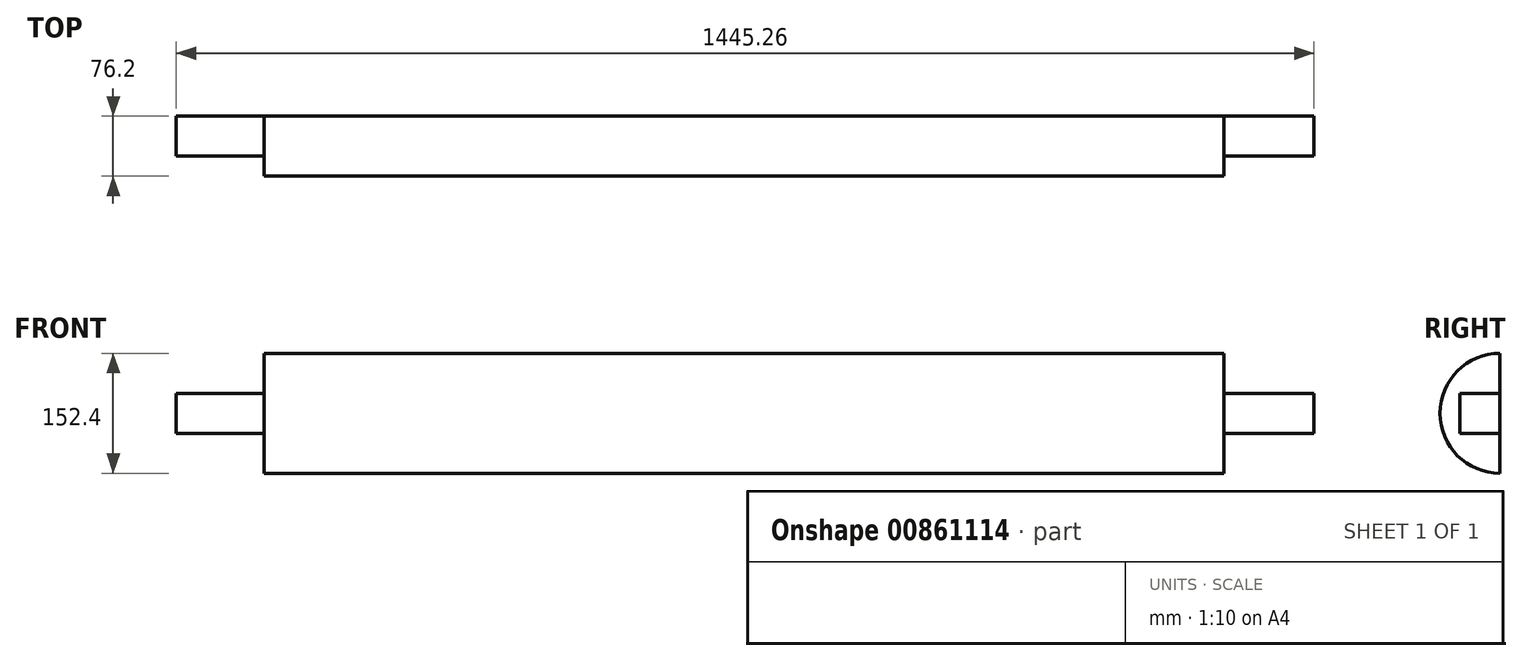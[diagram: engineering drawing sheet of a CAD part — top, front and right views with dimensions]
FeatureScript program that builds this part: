
annotation { "Feature Type Name" : "Feature", "Feature Type Description" : "" }
export const myFeature = defineFeature(function(context is Context, id is Id, definition is map)
    precondition{}
    {
        {
            var Q0;
            Q0=qCreatedBy(makeId("Right.planeOp"),FACE);
            var sketch = newSketch(context, id + "F0", { "sketchPlane" : qUnion([Q0])});
            skCircle(sketch, "E0", {"center": v(-55.26, 16.13) * mm, "radius": 76.2 * mm});
            skLineSegment(sketch, "E1", {"start": v(-55.26, 16.13) * mm, "end": v(-55.26, -60.07) * mm});
            skLineSegment(sketch, "E2", {"start": v(-55.26, -60.07) * mm, "end": v(-55.26, 92.33) * mm});
            skSolve(sketch);
        }
        {
            var Q0;
            {var subQ0=sQuery(id+"F0.wireOp",EDGE,"E2");var subQ4=makeQuery(id+"F0.imprint","IMPRINT",VERTEX,{"derivedFrom":subQ0});Q0=makeQuery(id+"F0.imprint","IMPRINT",FACE,{"disambiguationData":[TD([[makeQuery(id+"F0.imprint","IMPRINT",EDGE,{"disambiguationData":[TD([[subQ4,1.0]])],"derivedFrom":subQ0}),1.0]])]});}
            extrude(context, id + "F1", {"entities" : qUnion([Q0]), "depth" : 1219.2 * mm, "offsetDistance" : 25.4 * mm});
        }
        {
            var Q0;
            Q0=makeQuery(id+"F1.opExtrude","CAP_FACE",FACE,{"disambiguationData":[OSD([sQuery(id+"F0.wireOp",EDGE,"E0"),sQuery(id+"F0.wireOp",EDGE,"E2")])],"isStart":false});
            var sketch = newSketch(context, id + "F2", { "sketchPlane" : qUnion([Q0])});
            skLineSegment(sketch, "E3.bottom", {"start": v(-55.26, 41.38) * mm, "end": v(-106.06, 41.38) * mm});
            skLineSegment(sketch, "E3.top", {"start": v(-55.26, -9.42) * mm, "end": v(-106.06, -9.42) * mm});
            skLineSegment(sketch, "E3.left", {"start": v(-55.26, 41.38) * mm, "end": v(-55.26, -9.42) * mm});
            skLineSegment(sketch, "E3.right", {"start": v(-106.06, 41.38) * mm, "end": v(-106.06, -9.42) * mm});
            skPoint(sketch, "E3.middle", {"position": v(-80.66, 15.98) * mm});
            skPoint(sketch, "E4", {"position": v(-55.26, 15.98) * mm});
            skSolve(sketch);
        }
        {
            var Q0;
            Q0=makeQuery(id+"F2.imprint","IMPRINT",FACE,{"disambiguationData":[TD([[makeQuery(id+"F2.imprint","IMPRINT",EDGE,{"derivedFrom":sQuery(id+"F2.wireOp",EDGE,"E3.bottom")}),1.0]])]});
            extrude(context, id + "F3", {"entities" : qUnion([Q0]), "operationType" : NewBodyOperationType.ADD, "depth" : 114.3 * mm, "offsetDistance" : 25.4 * mm, "hasSecondDirection" : true, "secondDirectionOppositeDirection" : true, "secondDirectionDepth" : 1330.96 * mm});
        }
    });
